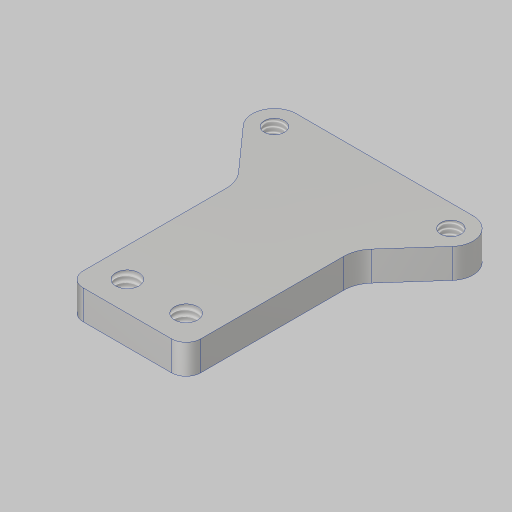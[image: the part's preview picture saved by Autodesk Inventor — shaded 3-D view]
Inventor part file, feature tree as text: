
AUTODESK INVENTOR PART (.ipt)
format: ipt  version: 2023.5 (Build 275446000, 446)  size: 648,704 bytes
history: native  units: in
note: dims shown in document units (in); Inventor stores cm internally (conversion verified against a paired STEP export)
features: other x8, fillet x6, extrude x5, sketch x3, hole x2, projected_geometry x1
ambient origin geometry x8: Origin, YZ Plane, XZ Plane, XY Plane, X Axis, Y Axis, Z Axis, Center Point
bodies: Solid1 (feature_tree)
feature tree (25):
  sketch  "Sketch1"  dims[d1=0.7in d3=0.13in]
  extrude  "Extrusion1"  Depth=0.13in
  hole  "Hole1"  [1 undecoded]
  fillet  "Fillet1"  Radius=1.0in
  extrude  "Extrusion2"  Depth=0.25in
  other  "Full Round Fillet1"
  other  "Full Round Fillet2"
  other  "Full Round Fillet3"
  other  "Full Round Fillet4"
  other  "Full Round Fillet5"
  other  "Full Round Fillet6"
  other  "Full Round Fillet7"
  fillet  "Fillet3"  Radius=0.5in
  sketch  "Sketch4"  dims[d4=0.197in d5=0.197in d8=1.0in]
  extrude  "Extrusion5"  Depth=0.25in
  hole  "Hole2"  [1 undecoded]
  extrude  "Extrusion6"  Depth=0.125in
  fillet  "Fillet4"  Radius=0.7874in
  fillet  "Fillet5"  Radius=1.5748in
  fillet  "Fillet6"  Radius=0.17in
  extrude  "Extrusion7"  Depth=0.0625in
  other  "Full Round Fillet8"
  fillet  "Fillet7"  Radius=1.5in
  sketch  "Sketch5"  dims[d9=2.0in d10=0.25in d11=0.5in d12=0.25in d13=0.25in d14=0.0in d15=0.196in d16=0.5in d17=0.385in d18=0.25in d19=0.5635in d20=1.0in d21=0.8108in d22=0.125in d23=0.7874in d25=0.197in d26=0.3937in d28=1.0in d30=1.5748in d32=0.197in d33=0.3937in d35=1.0in d37=0.17in d38=0.0in d43=0.0625in d50=1.5in d51=0.375in d52=0.75in d53=1.0in d54=0.0in d55=0.171in d56=0.432in d57=0.385in d58=0.25in d59=0.5635in d60=1.0in d61=0.8108in d62=0.125in d63=0.06in d64=0.0in d65=0.26in d66=0.13in d67=0.0625in d68=0.7874in d70=0.197in d71=0.3937in d73=1.0in d75=0.17in d76=0.0in d77=0.0625in]
  projected_geometry  "Project Cut Edges2"
note: 2 required parameter values undecoded (feature->parameter linkage not recoverable at this tier; creation-order binding heuristic only, values carry confidence <= 0.55)
